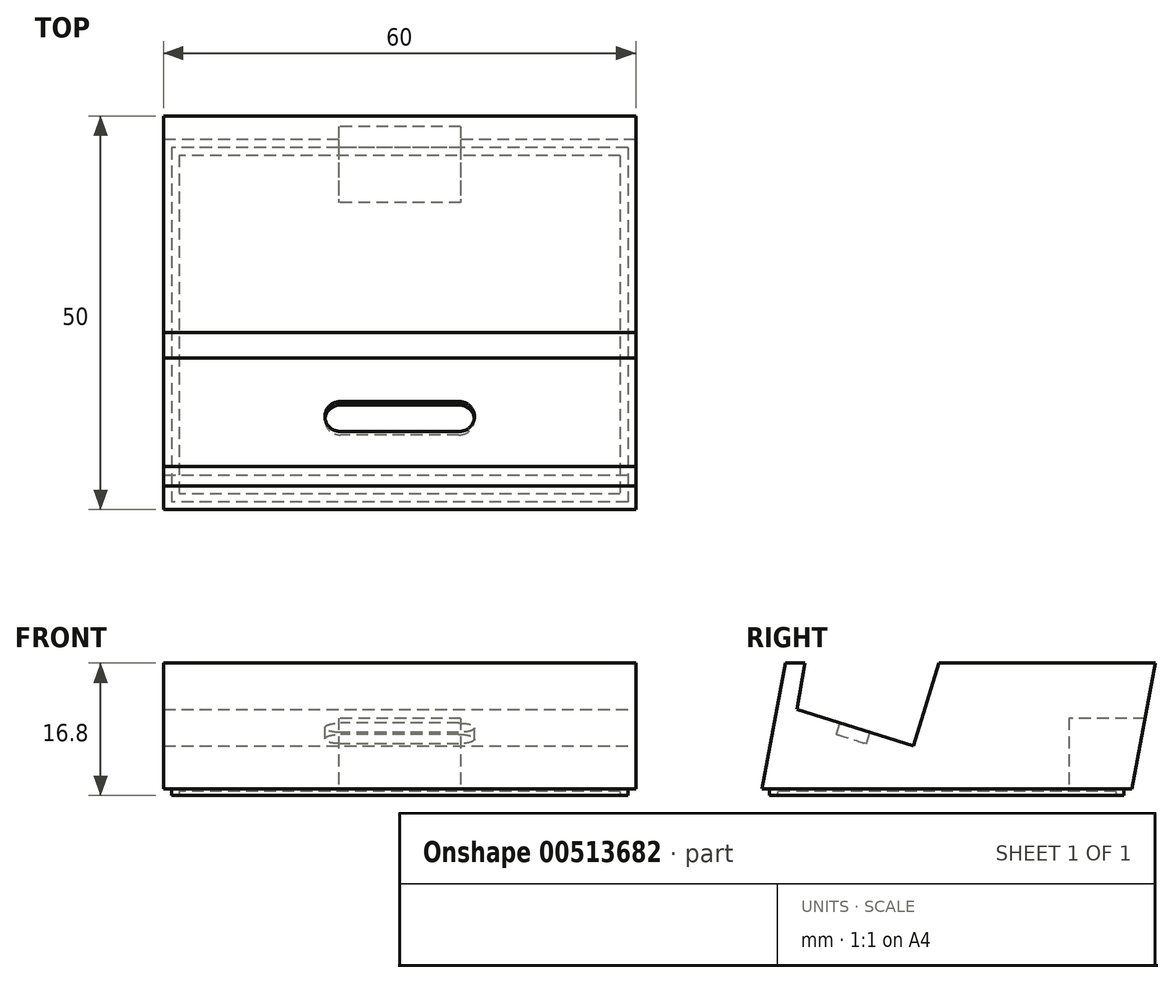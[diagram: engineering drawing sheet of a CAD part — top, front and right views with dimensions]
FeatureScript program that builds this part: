
annotation { "Feature Type Name" : "Feature", "Feature Type Description" : "" }
export const myFeature = defineFeature(function(context is Context, id is Id, definition is map)
    precondition{}
    {
        {
            var Q0;
            Q0=qCreatedBy(makeId("Top.planeOp"),FACE);
            var sketch = newSketch(context, id + "F0", { "sketchPlane" : qUnion([Q0])});
            skLineSegment(sketch, "E0.bottom", {"start": v(30, -23.5) * mm, "end": v(-30, -23.5) * mm});
            skLineSegment(sketch, "E0.top", {"start": v(30, 23.5) * mm, "end": v(-30, 23.5) * mm});
            skLineSegment(sketch, "E0.left", {"start": v(30, -23.5) * mm, "end": v(30, 23.5) * mm});
            skLineSegment(sketch, "E0.right", {"start": v(-30, -23.5) * mm, "end": v(-30, 23.5) * mm});
            skPoint(sketch, "E0.middle", {"position": v(0, 0) * mm});
            skSolve(sketch);
        }
        {
            var Q0;
            Q0 = qSketchRegion(id + "F0", true);
            extrude(context, id + "F1", {"entities" : qUnion([Q0]), "depth" : 16 * mm});
        }
        {
            var Q0;
            Q0=makeQuery(id+"F1.opExtrude","CAP_FACE",FACE,{"disambiguationData":[OSD([sQuery(id+"F0.wireOp",EDGE,"E0.bottom"),sQuery(id+"F0.wireOp",EDGE,"E0.top"),sQuery(id+"F0.wireOp",EDGE,"E0.left"),sQuery(id+"F0.wireOp",EDGE,"E0.right")])],"isStart":true});
            var sketch = newSketch(context, id + "F2", { "sketchPlane" : qUnion([Q0])});
            skLineSegment(sketch, "E1.bottom", {"start": v(29, -22.5) * mm, "end": v(-29, -22.5) * mm});
            skLineSegment(sketch, "E1.top", {"start": v(29, 22.5) * mm, "end": v(-29, 22.5) * mm});
            skLineSegment(sketch, "E1.left", {"start": v(29, -22.5) * mm, "end": v(29, 22.5) * mm});
            skLineSegment(sketch, "E1.right", {"start": v(-29, -22.5) * mm, "end": v(-29, 22.5) * mm});
            skPoint(sketch, "E1.middle", {"position": v(0, 0) * mm});
            skSolve(sketch);
        }
        {
            var Q0;
            Q0 = qSketchRegion(id + "F2", true);
            extrude(context, id + "F3", {"entities" : qUnion([Q0]), "operationType" : NewBodyOperationType.ADD, "depth" : 0.8 * mm});
        }
        {
            var Q0;
            Q0=makeQuery(id+"F3.opExtrude","CAP_FACE",FACE,{"disambiguationData":[OSD([sQuery(id+"F2.wireOp",EDGE,"E1.bottom"),sQuery(id+"F2.wireOp",EDGE,"E1.top"),sQuery(id+"F2.wireOp",EDGE,"E1.left"),sQuery(id+"F2.wireOp",EDGE,"E1.right")])],"isStart":false});
            var sketch = newSketch(context, id + "F4", { "sketchPlane" : qUnion([Q0])});
            skLineSegment(sketch, "E2.bottom", {"start": v(28, -21.5) * mm, "end": v(-28, -21.5) * mm});
            skLineSegment(sketch, "E2.top", {"start": v(28, 21.5) * mm, "end": v(-28, 21.5) * mm});
            skLineSegment(sketch, "E2.left", {"start": v(28, -21.5) * mm, "end": v(28, 21.5) * mm});
            skLineSegment(sketch, "E2.right", {"start": v(-28, -21.5) * mm, "end": v(-28, 21.5) * mm});
            skPoint(sketch, "E2.middle", {"position": v(0, 0) * mm});
            skSolve(sketch);
        }
        {
            var Q0;
            Q0=makeQuery(id+"F4.imprint","IMPRINT",FACE,{"disambiguationData":[TD([[makeQuery(id+"F4.imprint","IMPRINT",EDGE,{"derivedFrom":sQuery(id+"F4.wireOp",EDGE,"E2.bottom")}),-1.0]])]});
            extrude(context, id + "F5", {"entities" : qUnion([Q0]), "operationType" : NewBodyOperationType.REMOVE, "oppositeDirection" : true, "depth" : 0.5 * mm});
        }
        {
            var Q0;
            Q0=makeQuery(id+"F1.opExtrude","SWEPT_FACE",FACE,{"disambiguationData":[OSD([sQuery(id+"F0.wireOp",EDGE,"E0.left")])]});
            var sketch = newSketch(context, id + "F6", { "sketchPlane" : qUnion([Q0])});
            skLineSegment(sketch, "E3", {"start": v(23.5, 16) * mm, "end": v(26.5, 16) * mm});
            skLineSegment(sketch, "E4", {"start": v(26.5, 16) * mm, "end": v(23.5, 0) * mm});
            skSolve(sketch);
        }
        {
            var Q0;
            Q0 = qSketchRegion(id + "F6", true);
            var Q1;
            Q1=makeQuery(id+"F6.imprint","IMPRINT",FACE,{"disambiguationData":[TD([[makeQuery(id+"F6.imprint","IMPRINT",EDGE,{"derivedFrom":sQuery(id+"F6.wireOp",EDGE,"E3")}),-1.0]])]});
            extrude(context, id + "F7", {"entities" : qUnion([Q0, Q1]), "operationType" : NewBodyOperationType.ADD, "oppositeDirection" : true, "depth" : 60 * mm});
        }
        {
            var Q0;
            {var subQ0=sQuery(id+"F0.wireOp",EDGE,"E0.left");Q0=makeQuery(id+"F7.boolean.opBoolean","MERGE",FACE,{"derivedFrom":[makeQuery(id+"F1.opExtrude","SWEPT_FACE",FACE,{"disambiguationData":[OSD([subQ0])]}),makeQuery(id+"F7.opExtrude","CAP_FACE",FACE,{"disambiguationData":[OSD([sQuery(id+"F0.wireOp",EDGE,"E0.top"),subQ0,sQuery(id+"F6.wireOp",EDGE,"E3"),sQuery(id+"F6.wireOp",EDGE,"E4")])],"isStart":true})]});}
            var sketch = newSketch(context, id + "F8", { "sketchPlane" : qUnion([Q0])});
            skLineSegment(sketch, "E5", {"start": v(-23.5, 16) * mm, "end": v(-20.5, 16) * mm});
            skLineSegment(sketch, "E6", {"start": v(-20.5, 16) * mm, "end": v(-23.5, 0) * mm});
            skSolve(sketch);
        }
        {
            var Q0;
            Q0 = qSketchRegion(id + "F8", true);
            var Q1;
            Q1=makeQuery(id+"F8.imprint","IMPRINT",FACE,{"disambiguationData":[TD([[makeQuery(id+"F8.imprint","IMPRINT",EDGE,{"derivedFrom":sQuery(id+"F8.wireOp",EDGE,"E5")}),-1.0]])]});
            extrude(context, id + "F9", {"entities" : qUnion([Q0, Q1]), "operationType" : NewBodyOperationType.REMOVE, "endBound" : BoundingType.THROUGH_ALL, "oppositeDirection" : true, "depth" : 25 * mm});
        }
        {
            var Q0;
            {var subQ0=sQuery(id+"F0.wireOp",EDGE,"E0.left");Q0=makeQuery(id+"F7.boolean.opBoolean","MERGE",FACE,{"derivedFrom":[makeQuery(id+"F1.opExtrude","SWEPT_FACE",FACE,{"disambiguationData":[OSD([subQ0])]}),makeQuery(id+"F7.opExtrude","CAP_FACE",FACE,{"disambiguationData":[OSD([sQuery(id+"F0.wireOp",EDGE,"E0.top"),subQ0,sQuery(id+"F6.wireOp",EDGE,"E3"),sQuery(id+"F6.wireOp",EDGE,"E4")])],"isStart":true})]});}
            var sketch = newSketch(context, id + "F10", { "sketchPlane" : qUnion([Q0])});
            skLineSegment(sketch, "E7", {"start": v(-1, 16) * mm, "end": v(-4.26, 5.5) * mm});
            skLineSegment(sketch, "E8", {"start": v(-19.06, 10.1) * mm, "end": v(-18, 16) * mm});
            skLineSegment(sketch, "E9", {"start": v(-19.06, 10.1) * mm, "end": v(-4.26, 5.5) * mm});
            skSolve(sketch);
        }
        {
            var Q0;
            Q0 = qSketchRegion(id + "F10", true);
            var Q1;
            {var subQ0=sQuery(id+"F10.wireOp",EDGE,"E7");Q1=makeQuery(id+"F10.imprint","IMPRINT",FACE,{"disambiguationData":[TD([[makeQuery(id+"F10.imprint","IMPRINT",EDGE,{"derivedFrom":subQ0}),-1.0]])]});}
            extrude(context, id + "F11", {"entities" : qUnion([Q0, Q1]), "operationType" : NewBodyOperationType.REMOVE, "endBound" : BoundingType.THROUGH_ALL, "oppositeDirection" : true, "depth" : 25 * mm});
        }
        {
            var Q0;
            Q0=qCreatedBy(makeId("Right.planeOp"),FACE);
            var sketch = newSketch(context, id + "F12", { "sketchPlane" : qUnion([Q0])});
            skPoint(sketch, "E10", {"position": v(15.5, 0) * mm});
            skSolve(sketch);
        }
        {
            var Q0;
            Q0=sQuery(id+"F12.wireOp",VERTEX,"E10");
            var Q1;
            Q1=qCreatedBy(makeId("Front.planeOp"),FACE);
            cPlane(context, id + "F13", {"entities" : qUnion([Q0, Q1]), "cplaneType" : CPlaneType.PLANE_POINT, "offset" : 25 * mm, "width" : 150 * mm, "height" : 150 * mm});
        }
        {
            var Q0;
            Q0=qCreatedBy(id+"F13.planeOp",FACE);
            var sketch = newSketch(context, id + "F14", { "sketchPlane" : qUnion([Q0])});
            skLineSegment(sketch, "E11.bottom", {"start": v(7.75, 9) * mm, "end": v(-7.75, 9) * mm});
            skLineSegment(sketch, "E12", {"start": v(-7.75, 9) * mm, "end": v(-7.75, 0) * mm});
            skLineSegment(sketch, "E13", {"start": v(7.75, 9) * mm, "end": v(7.75, 0) * mm});
            skLineSegment(sketch, "E14", {"start": v(7.75, 0) * mm, "end": v(-7.75, 0) * mm});
            skSolve(sketch);
        }
        {
            var Q0;
            Q0 = qSketchRegion(id + "F14", true);
            extrude(context, id + "F15", {"entities" : qUnion([Q0]), "operationType" : NewBodyOperationType.REMOVE, "oppositeDirection" : true, "depth" : 25 * mm});
        }
        {
            var Q0;
            Q0=makeQuery(id+"F11.boolean.opBoolean","COPY",FACE,{"derivedFrom":makeQuery(id+"F11.opExtrude","SWEPT_FACE",FACE,{"disambiguationData":[OSD([sQuery(id+"F10.wireOp",EDGE,"E9")])]})});
            var sketch = newSketch(context, id + "F16", { "sketchPlane" : qUnion([Q0])});
            skPoint(sketch, "E15.startSnap0", {"position": v(0, -5.7) * mm});
            skPoint(sketch, "E15.startSnap1", {"position": v(-30, -13.45) * mm});
            skLineSegment(sketch, "E16", {"start": v(7.5, -13.45) * mm, "end": v(-7.5, -13.45) * mm});
            skArc(sketch, "E17.0.startCap", {"start": v(7.5, -11.45) * mm, "mid": v(9.5, -13.45) * mm, "end": v(7.5, -15.45) * mm});
            skArc(sketch, "E17.0.endCap", {"start": v(-7.5, -15.45) * mm, "mid": v(-9.5, -13.45) * mm, "end": v(-7.5, -11.45) * mm});
            skLineSegment(sketch, "E17.0.left", {"start": v(7.5, -15.45) * mm, "end": v(-7.5, -15.45) * mm});
            skLineSegment(sketch, "E17.0.right", {"start": v(7.5, -11.45) * mm, "end": v(-7.5, -11.45) * mm});
            skSolve(sketch);
        }
        {
            var Q0;
            Q0 = qSketchRegion(id + "F16", true);
            var Q1;
            Q1=makeQuery(id+"F9.boolean.opBoolean","COPY",FACE,{"derivedFrom":makeQuery(id+"F9.opExtrude","SWEPT_FACE",FACE,{"disambiguationData":[OSD([sQuery(id+"F8.wireOp",EDGE,"E6")])]})});
            extrude(context, id + "F17", {"entities" : qUnion([Q0, Q1]), "operationType" : NewBodyOperationType.REMOVE, "oppositeDirection" : true, "depth" : 1.5 * mm, "offsetDistance" : 25 * mm});
        }
    });
